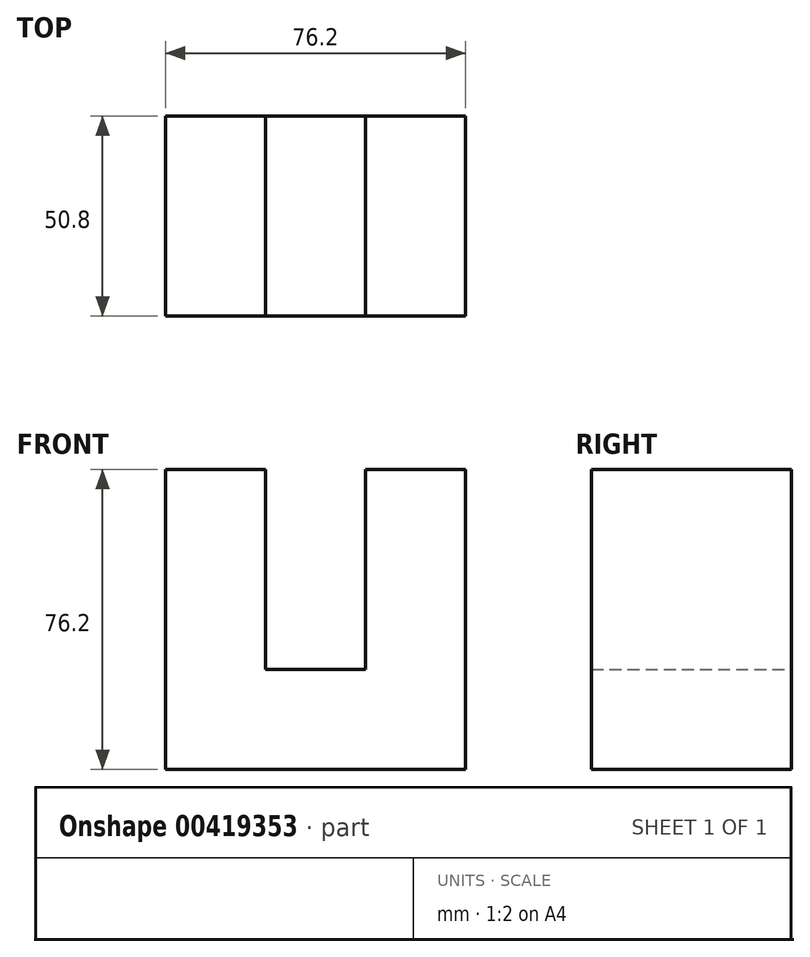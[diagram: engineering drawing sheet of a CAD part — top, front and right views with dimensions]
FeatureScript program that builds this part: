
annotation { "Feature Type Name" : "Feature", "Feature Type Description" : "" }
export const myFeature = defineFeature(function(context is Context, id is Id, definition is map)
    precondition{}
    {
        {
            var Q0;
            Q0=qCreatedBy(makeId("Front.planeOp"),FACE);
            var sketch = newSketch(context, id + "F0", { "sketchPlane" : qUnion([Q0])});
            skLineSegment(sketch, "E0", {"start": v(-4.96, 50.8) * mm, "end": v(-30.36, 50.8) * mm});
            skLineSegment(sketch, "E1", {"start": v(-30.36, 50.8) * mm, "end": v(-30.36, -25.4) * mm});
            skLineSegment(sketch, "E2", {"start": v(-30.36, -25.4) * mm, "end": v(45.84, -25.4) * mm});
            skLineSegment(sketch, "E3", {"start": v(45.84, -25.4) * mm, "end": v(45.84, 50.8) * mm});
            skLineSegment(sketch, "E4", {"start": v(45.84, 50.8) * mm, "end": v(20.44, 50.8) * mm});
            skLineSegment(sketch, "E5", {"start": v(20.44, 50.8) * mm, "end": v(20.44, 0) * mm});
            skLineSegment(sketch, "E6", {"start": v(20.44, 0) * mm, "end": v(-4.96, 0) * mm});
            skLineSegment(sketch, "E7", {"start": v(-4.96, 0) * mm, "end": v(-4.96, 50.8) * mm});
            skSolve(sketch);
        }
        {
            var Q0;
            Q0 = qSketchRegion(id + "F0", true);
            extrude(context, id + "F1", {"entities" : qUnion([Q0]), "depth" : 50.8 * mm});
        }
    });
